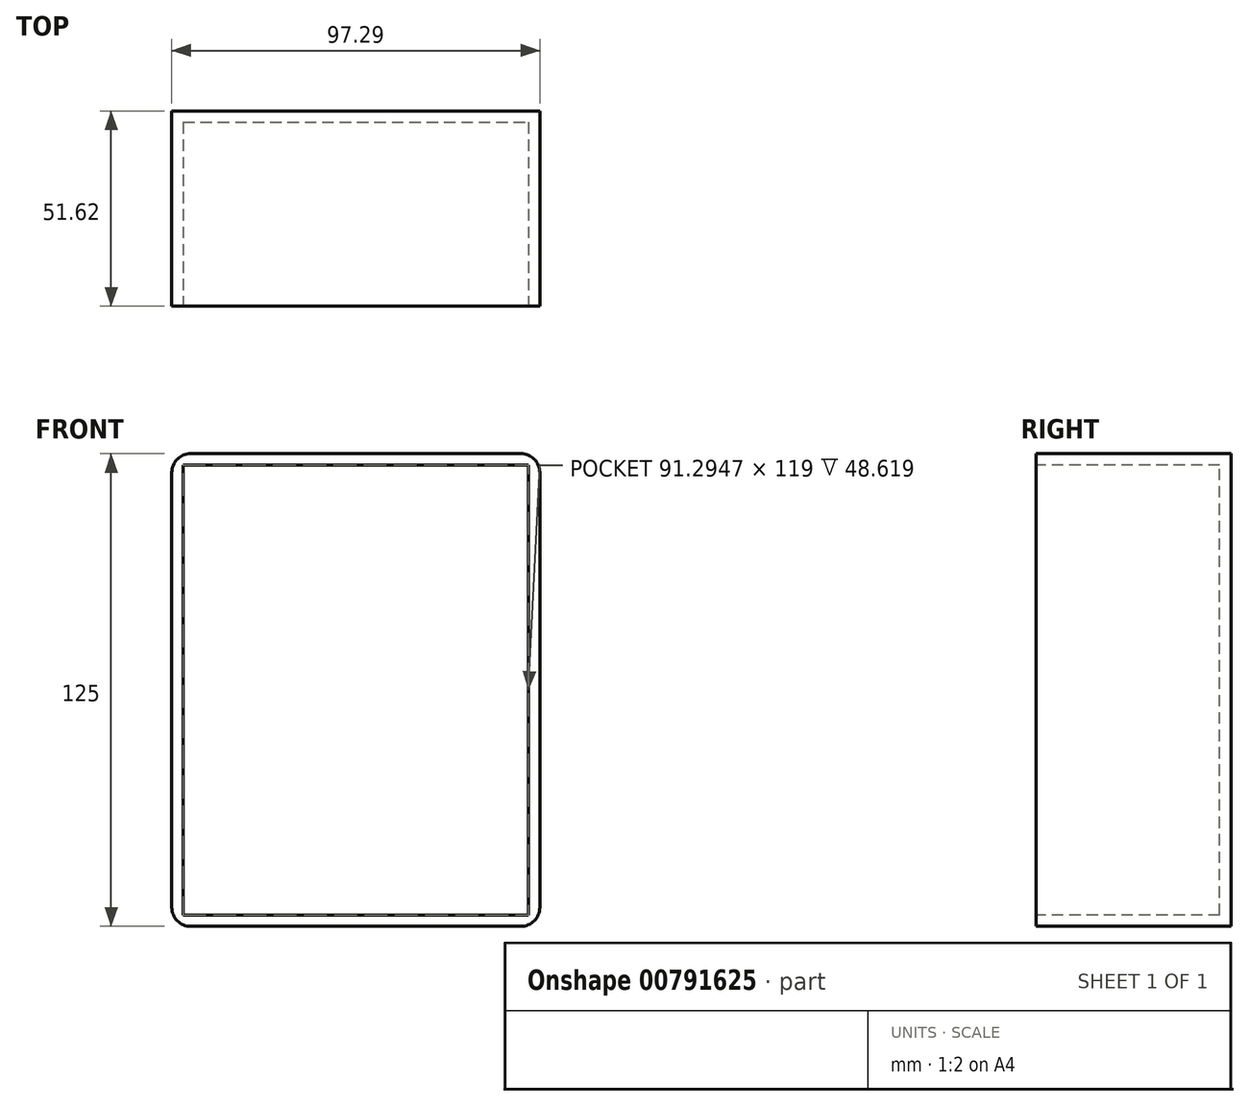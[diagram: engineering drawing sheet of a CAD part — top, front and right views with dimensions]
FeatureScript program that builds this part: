
annotation { "Feature Type Name" : "Feature", "Feature Type Description" : "" }
export const myFeature = defineFeature(function(context is Context, id is Id, definition is map)
    precondition{}
    {
        {
            var Q0;
            Q0=qCreatedBy(makeId("Top.planeOp"),FACE);
            var sketch = newSketch(context, id + "F0", { "sketchPlane" : qUnion([Q0])});
            skLineSegment(sketch, "E0", {"start": v(0, 0) * mm, "end": v(0, -51.62) * mm});
            skLineSegment(sketch, "E1", {"start": v(0, -51.62) * mm, "end": v(97.3, -51.62) * mm});
            skLineSegment(sketch, "E2", {"start": v(97.3, -51.62) * mm, "end": v(97.3, 0) * mm});
            skLineSegment(sketch, "E3", {"start": v(97.3, 0) * mm, "end": v(0, 0) * mm});
            skSolve(sketch);
        }
        {
            var Q0;
            Q0=makeQuery(id+"F0.imprint","IMPRINT",FACE,{"disambiguationData":[TD([[makeQuery(id+"F0.imprint","IMPRINT",EDGE,{"derivedFrom":sQuery(id+"F0.wireOp",EDGE,"E0")}),1.0]])]});
            extrude(context, id + "F1", {"entities" : qUnion([Q0]), "depth" : 25 * mm, "offsetDistance" : 25 * mm});
        }
        {
            var Q0;
            Q0=makeQuery(id+"F1.opExtrude","CAP_FACE",FACE,{"disambiguationData":[OSD([sQuery(id+"F0.wireOp",EDGE,"E0"),sQuery(id+"F0.wireOp",EDGE,"E1"),sQuery(id+"F0.wireOp",EDGE,"E2"),sQuery(id+"F0.wireOp",EDGE,"E3")])],"isStart":false});
            extrude(context, id + "F2", {"entities" : qUnion([Q0]), "operationType" : NewBodyOperationType.ADD, "depth" : 100 * mm, "offsetDistance" : 25 * mm});
        }
        {
            var Q0;
            {var subQ0=sQuery(id+"F0.wireOp",EDGE,"E1");Q0=makeQuery(id+"F2.boolean.opBoolean","MERGE",FACE,{"derivedFrom":[makeQuery(id+"F1.opExtrude","SWEPT_FACE",FACE,{"disambiguationData":[OSD([subQ0])]}),makeQuery(id+"F2.opExtrude","SWEPT_FACE",FACE,{"disambiguationData":[OSD([subQ0])]})]});}
            var sketch = newSketch(context, id + "F3", { "sketchPlane" : qUnion([Q0])});
            skLineSegment(sketch, "E4.bottom", {"start": v(94.3, 122) * mm, "end": v(3, 122) * mm});
            skLineSegment(sketch, "E4.top", {"start": v(94.3, 3) * mm, "end": v(3, 3) * mm});
            skLineSegment(sketch, "E4.left", {"start": v(94.3, 122) * mm, "end": v(94.3, 3) * mm});
            skLineSegment(sketch, "E4.right", {"start": v(3, 122) * mm, "end": v(3, 3) * mm});
            skPoint(sketch, "E4.middle", {"position": v(48.65, 62.5) * mm});
            skSolve(sketch);
        }
        {
            var Q0;
            Q0 = qSketchRegion(id + "F3", true);
            var Q1;
            {var subQ0=sQuery(id+"F0.wireOp",EDGE,"E3");Q1=makeQuery(id+"F2.boolean.opBoolean","MERGE",FACE,{"derivedFrom":[makeQuery(id+"F1.opExtrude","SWEPT_FACE",FACE,{"disambiguationData":[OSD([subQ0])]}),makeQuery(id+"F2.opExtrude","SWEPT_FACE",FACE,{"disambiguationData":[OSD([subQ0])]})]});}
            extrude(context, id + "F4", {"entities" : qUnion([Q0]), "operationType" : NewBodyOperationType.REMOVE, "endBound" : BoundingType.UP_TO_SURFACE, "oppositeDirection" : true, "depth" : 47 * mm, "endBoundEntityFace" : qUnion([Q1]), "hasOffset" : true, "offsetDistance" : 3 * mm});
        }
        {
            var Q0;
            Q0=makeQuery(id+"F2.opExtrude","CAP_EDGE",EDGE,{"disambiguationData":[OSD([sQuery(id+"F0.wireOp",EDGE,"E2")])],"isStart":false});
            var Q1;
            Q1=makeQuery(id+"F2.opExtrude","CAP_EDGE",EDGE,{"disambiguationData":[OSD([sQuery(id+"F0.wireOp",EDGE,"E0")])],"isStart":false});
            var Q2;
            Q2=makeQuery(id+"F1.opExtrude","CAP_EDGE",EDGE,{"disambiguationData":[OSD([sQuery(id+"F0.wireOp",EDGE,"E0")])],"isStart":true});
            var Q3;
            Q3=makeQuery(id+"F1.opExtrude","CAP_EDGE",EDGE,{"disambiguationData":[OSD([sQuery(id+"F0.wireOp",EDGE,"E2")])],"isStart":true});
            fillet(context, id + "F5", {"entities" : qUnion([Q0, Q1, Q2, Q3]), "radius" : 5 * mm, "tangentPropagation" : true, "allowEdgeOverflow" : false});
        }
    });
